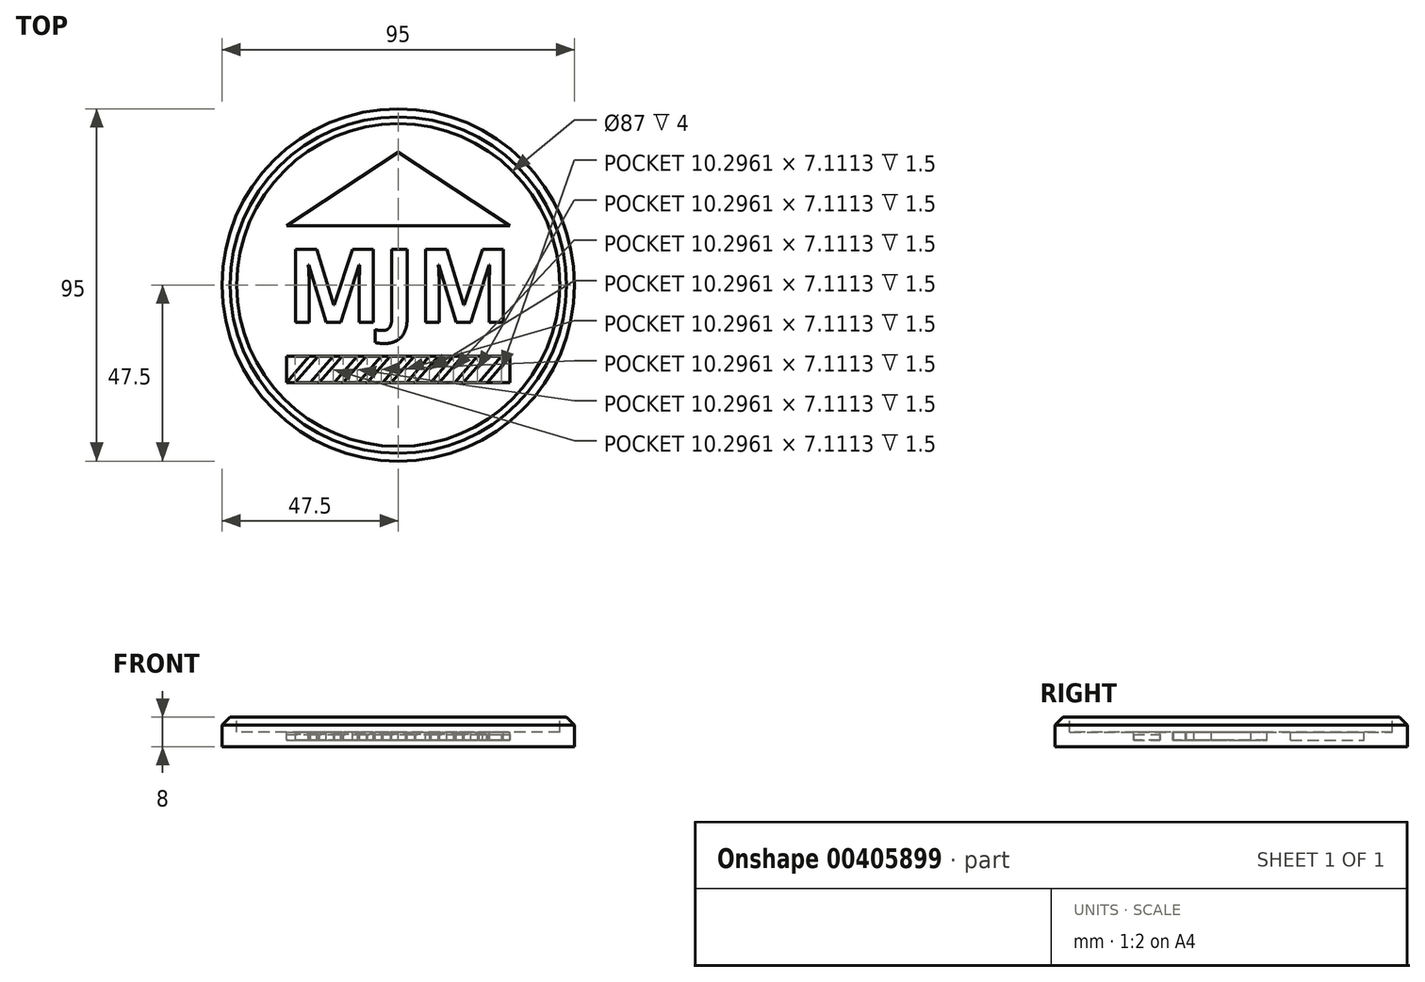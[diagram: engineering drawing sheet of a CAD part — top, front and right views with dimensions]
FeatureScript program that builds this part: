
annotation { "Feature Type Name" : "Feature", "Feature Type Description" : "" }
export const myFeature = defineFeature(function(context is Context, id is Id, definition is map)
    precondition{}
    {
        {
            var Q0;
            Q0=qCreatedBy(makeId("Top.planeOp"),FACE);
            var sketch = newSketch(context, id + "F0", { "sketchPlane" : qUnion([Q0])});
            skCircle(sketch, "E0", {"center": v(0, 0) * mm, "radius": 47.5 * mm});
            skSolve(sketch);
        }
        {
            var Q0;
            Q0=makeQuery(id+"F0.imprint","IMPRINT",FACE,{"disambiguationData":[TD([[makeQuery(id+"F0.imprint","IMPRINT",EDGE,{"derivedFrom":sQuery(id+"F0.wireOp",EDGE,"E0")}),1.0]])]});
            extrude(context, id + "F1", {"entities" : qUnion([Q0]), "depth" : 8 * mm});
        }
        {
            var Q0;
            Q0=makeQuery(id+"F1.opExtrude","CAP_FACE",FACE,{"disambiguationData":[OSD([sQuery(id+"F0.wireOp",EDGE,"E0")])],"isStart":false});
            var sketch = newSketch(context, id + "F2", { "sketchPlane" : qUnion([Q0])});
            skCircle(sketch, "E1", {"center": v(0, 0) * mm, "radius": 43.5 * mm});
            skSolve(sketch);
        }
        {
            var Q0;
            Q0=makeQuery(id+"F2.imprint","IMPRINT",FACE,{"disambiguationData":[TD([[makeQuery(id+"F2.imprint","IMPRINT",EDGE,{"derivedFrom":sQuery(id+"F2.wireOp",EDGE,"E1")}),1.0]])]});
            extrude(context, id + "F3", {"entities" : qUnion([Q0]), "operationType" : NewBodyOperationType.REMOVE, "oppositeDirection" : true, "depth" : 4 * mm});
        }
        {
            var Q0;
            Q0=makeQuery(id+"F3.boolean.opBoolean","COPY",FACE,{"derivedFrom":makeQuery(id+"F3.opExtrude","CAP_FACE",FACE,{"disambiguationData":[OSD([sQuery(id+"F2.wireOp",EDGE,"E1")])],"isStart":false})});
            var sketch = newSketch(context, id + "F4", { "sketchPlane" : qUnion([Q0])});
            skText(sketch, "E2", { "text": "MJM", "fontName": "OpenSans-Bold.ttf"});
            skLineSegment(sketch, "E3", {"start": v(-30.16, 16.03) * mm, "end": v(0, 35.84) * mm});
            skLineSegment(sketch, "E4", {"start": v(0, 35.84) * mm, "end": v(30.16, 16.03) * mm});
            skLineSegment(sketch, "E5", {"start": v(30.16, 16.03) * mm, "end": v(-30.16, 16.03) * mm});
            skLineSegment(sketch, "E6.bottom", {"start": v(-30.16, -19.19) * mm, "end": v(30.16, -19.19) * mm});
            skLineSegment(sketch, "E6.top", {"start": v(-30.16, -26.3) * mm, "end": v(30.16, -26.3) * mm});
            skLineSegment(sketch, "E6.left", {"start": v(-30.16, -19.19) * mm, "end": v(-30.16, -26.3) * mm});
            skLineSegment(sketch, "E6.right", {"start": v(30.16, -19.19) * mm, "end": v(30.16, -26.3) * mm});
            const initialGuessF4  = {"E2": [-0.03016, -0.01, 1, 0, 0.01981]};
            skSetInitialGuess(sketch, initialGuessF4);
            skSolve(sketch);
        }
        {
            var Q0;
            Q0 = qSketchRegion(id + "F4", true);
            extrude(context, id + "F5", {"entities" : qUnion([Q0]), "operationType" : NewBodyOperationType.REMOVE, "oppositeDirection" : true, "depth" : 2.25 * mm});
        }
        {
            var Q0;
            Q0=makeQuery(id+"F1.opExtrude","CAP_EDGE",EDGE,{"disambiguationData":[OSD([sQuery(id+"F0.wireOp",EDGE,"E0")])],"isStart":false});
            chamfer(context, id + "F6", {"entities" : qUnion([Q0]), "width" : 2.16 * mm, "tangentPropagation" : true});
        }
        {
            var Q0;
            Q0=makeQuery(id+"F5.boolean.opBoolean","COPY",FACE,{"derivedFrom":makeQuery(id+"F5.opExtrude","CAP_FACE",FACE,{"disambiguationData":[OSD([sQuery(id+"F4.wireOp",EDGE,"E6.bottom"),sQuery(id+"F4.wireOp",EDGE,"E6.top"),sQuery(id+"F4.wireOp",EDGE,"E6.left"),sQuery(id+"F4.wireOp",EDGE,"E6.right")])],"isStart":false})});
            var sketch = newSketch(context, id + "F7", { "sketchPlane" : qUnion([Q0])});
            skLineSegment(sketch, "E7", {"start": v(-30.16, -26.3) * mm, "end": v(-23.98, -19.19) * mm});
            skLineSegment(sketch, "E8", {"start": v(-23.98, -19.19) * mm, "end": v(-22.64, -20.35) * mm, "construction": true});
            skLineSegment(sketch, "E9", {"start": v(-30.16, -26.3) * mm, "end": v(-28.81, -27.47) * mm, "construction": true});
            skLineSegment(sketch, "E10", {"start": v(-22.64, -20.35) * mm, "end": v(-27.8, -26.3) * mm});
            skLineSegment(sketch, "E11", {"start": v(-22.64, -20.35) * mm, "end": v(-21.63, -19.19) * mm});
            skLineSegment(sketch, "E12", {"start": v(-23.98, -19.19) * mm, "end": v(-21.63, -19.19) * mm});
            skLineSegment(sketch, "E13", {"start": v(-30.16, -26.3) * mm, "end": v(-27.8, -26.3) * mm});
            skLineSegment(sketch, "E14.1.0.0", {"start": v(-16.16, -20.35) * mm, "end": v(-21.33, -26.3) * mm});
            skLineSegment(sketch, "E14.1.0.1", {"start": v(-23.68, -26.3) * mm, "end": v(-17.5, -19.19) * mm});
            skLineSegment(sketch, "E14.1.0.2", {"start": v(-17.5, -19.19) * mm, "end": v(-15.15, -19.19) * mm});
            skLineSegment(sketch, "E14.1.0.3", {"start": v(-16.16, -20.35) * mm, "end": v(-15.15, -19.19) * mm});
            skLineSegment(sketch, "E14.1.0.4", {"start": v(-23.68, -26.3) * mm, "end": v(-21.33, -26.3) * mm});
            skLineSegment(sketch, "E14.2.0.0", {"start": v(-9.69, -20.35) * mm, "end": v(-14.85, -26.3) * mm});
            skLineSegment(sketch, "E14.2.0.1", {"start": v(-17.2, -26.3) * mm, "end": v(-11.03, -19.19) * mm});
            skLineSegment(sketch, "E14.2.0.2", {"start": v(-11.03, -19.19) * mm, "end": v(-8.67, -19.19) * mm});
            skLineSegment(sketch, "E14.2.0.3", {"start": v(-9.69, -20.35) * mm, "end": v(-8.67, -19.19) * mm});
            skLineSegment(sketch, "E14.2.0.4", {"start": v(-17.2, -26.3) * mm, "end": v(-14.85, -26.3) * mm});
            skLineSegment(sketch, "E14.3.0.0", {"start": v(-3.2, -20.35) * mm, "end": v(-8.37, -26.3) * mm});
            skLineSegment(sketch, "E14.3.0.1", {"start": v(-10.73, -26.3) * mm, "end": v(-4.55, -19.19) * mm});
            skLineSegment(sketch, "E14.3.0.2", {"start": v(-4.55, -19.19) * mm, "end": v(-2.2, -19.19) * mm});
            skLineSegment(sketch, "E14.3.0.3", {"start": v(-3.2, -20.35) * mm, "end": v(-2.2, -19.19) * mm});
            skLineSegment(sketch, "E14.3.0.4", {"start": v(-10.73, -26.3) * mm, "end": v(-8.37, -26.3) * mm});
            skLineSegment(sketch, "E14.4.0.0", {"start": v(3.27, -20.35) * mm, "end": v(-1.9, -26.3) * mm});
            skLineSegment(sketch, "E14.4.0.1", {"start": v(-4.25, -26.3) * mm, "end": v(1.92, -19.19) * mm});
            skLineSegment(sketch, "E14.4.0.2", {"start": v(1.92, -19.19) * mm, "end": v(4.28, -19.19) * mm});
            skLineSegment(sketch, "E14.4.0.3", {"start": v(3.27, -20.35) * mm, "end": v(4.28, -19.19) * mm});
            skLineSegment(sketch, "E14.4.0.4", {"start": v(-4.25, -26.3) * mm, "end": v(-1.9, -26.3) * mm});
            skLineSegment(sketch, "E14.5.0.0", {"start": v(9.74, -20.35) * mm, "end": v(4.58, -26.3) * mm});
            skLineSegment(sketch, "E14.5.0.1", {"start": v(2.23, -26.3) * mm, "end": v(8.4, -19.19) * mm});
            skLineSegment(sketch, "E14.5.0.2", {"start": v(8.4, -19.19) * mm, "end": v(10.76, -19.19) * mm});
            skLineSegment(sketch, "E14.5.0.3", {"start": v(9.74, -20.35) * mm, "end": v(10.76, -19.19) * mm});
            skLineSegment(sketch, "E14.5.0.4", {"start": v(2.23, -26.3) * mm, "end": v(4.58, -26.3) * mm});
            skLineSegment(sketch, "E14.6.0.0", {"start": v(16.22, -20.35) * mm, "end": v(11.06, -26.3) * mm});
            skLineSegment(sketch, "E14.6.0.1", {"start": v(8.7, -26.3) * mm, "end": v(14.88, -19.19) * mm});
            skLineSegment(sketch, "E14.6.0.2", {"start": v(14.88, -19.19) * mm, "end": v(17.23, -19.19) * mm});
            skLineSegment(sketch, "E14.6.0.3", {"start": v(16.22, -20.35) * mm, "end": v(17.23, -19.19) * mm});
            skLineSegment(sketch, "E14.6.0.4", {"start": v(8.7, -26.3) * mm, "end": v(11.06, -26.3) * mm});
            skLineSegment(sketch, "E14.7.0.0", {"start": v(22.7, -20.35) * mm, "end": v(17.54, -26.3) * mm});
            skLineSegment(sketch, "E14.7.0.1", {"start": v(15.18, -26.3) * mm, "end": v(21.36, -19.19) * mm});
            skLineSegment(sketch, "E14.7.0.2", {"start": v(21.36, -19.19) * mm, "end": v(23.71, -19.19) * mm});
            skLineSegment(sketch, "E14.7.0.3", {"start": v(22.7, -20.35) * mm, "end": v(23.71, -19.19) * mm});
            skLineSegment(sketch, "E14.7.0.4", {"start": v(15.18, -26.3) * mm, "end": v(17.54, -26.3) * mm});
            skLineSegment(sketch, "E14.8.0.0", {"start": v(29.18, -20.35) * mm, "end": v(24.01, -26.3) * mm});
            skLineSegment(sketch, "E14.8.0.1", {"start": v(21.66, -26.3) * mm, "end": v(27.83, -19.19) * mm});
            skLineSegment(sketch, "E14.8.0.2", {"start": v(27.83, -19.19) * mm, "end": v(30.19, -19.19) * mm});
            skLineSegment(sketch, "E14.8.0.3", {"start": v(29.18, -20.35) * mm, "end": v(30.19, -19.19) * mm});
            skLineSegment(sketch, "E14.8.0.4", {"start": v(21.66, -26.3) * mm, "end": v(24.01, -26.3) * mm});
            skLineSegment(sketch, "E14.direction1", {"start": v(-27.8, -26.3) * mm, "end": v(-21.33, -26.3) * mm, "construction": true});
            skSolve(sketch);
        }
        {
            var Q0;
            Q0 = qSketchRegion(id + "F7", true);
            extrude(context, id + "F8", {"entities" : qUnion([Q0]), "operationType" : NewBodyOperationType.ADD, "depth" : 1.5 * mm});
        }
    });
